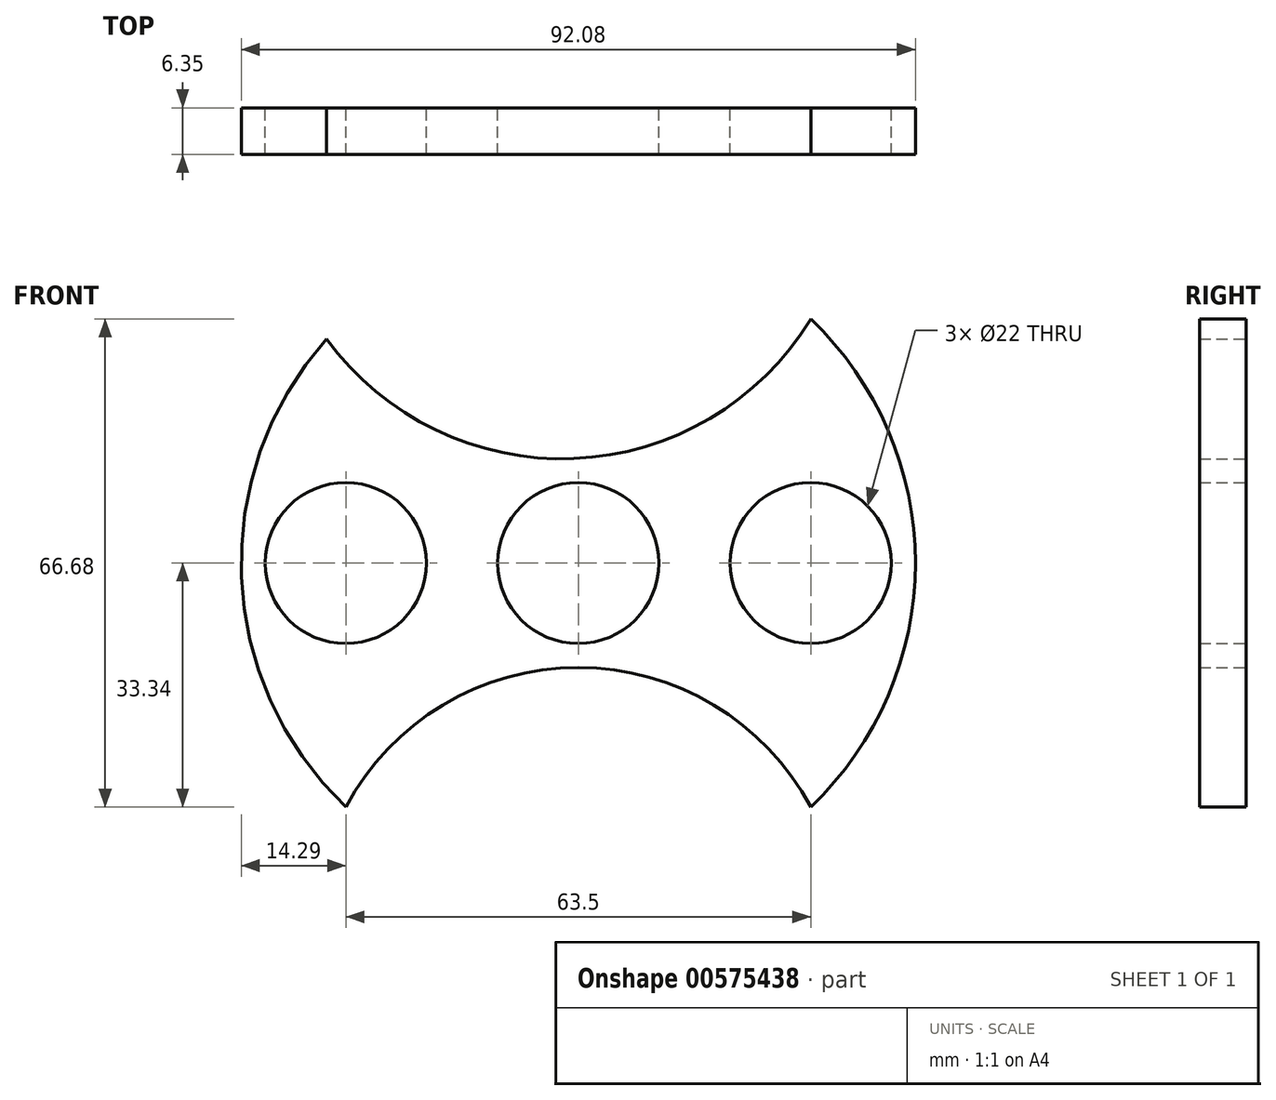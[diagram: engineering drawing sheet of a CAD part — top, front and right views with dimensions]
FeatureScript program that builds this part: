
annotation { "Feature Type Name" : "Feature", "Feature Type Description" : "" }
export const myFeature = defineFeature(function(context is Context, id is Id, definition is map)
    precondition{}
    {
        {
            var Q0;
            Q0=qCreatedBy(makeId("Front.planeOp"),FACE);
            var sketch = newSketch(context, id + "F0", { "sketchPlane" : qUnion([Q0])});
            skCircle(sketch, "E0", {"center": v(0, 0) * mm, "radius": 14.29 * mm});
            skCircle(sketch, "E1", {"center": v(0, 0) * mm, "radius": 11 * mm});
            skCircle(sketch, "E2", {"center": v(-31.75, 0) * mm, "radius": 14.29 * mm});
            skCircle(sketch, "E3", {"center": v(-31.75, 0) * mm, "radius": 11 * mm});
            skCircle(sketch, "E4.1.0", {"center": v(31.75, 0) * mm, "radius": 14.29 * mm});
            skCircle(sketch, "E4.1.1", {"center": v(31.75, 0) * mm, "radius": 11 * mm});
            skArc(sketch, "E5", {"start": v(-34.37, 30.63) * mm, "mid": v(-46, -1.88) * mm, "end": v(-31.75, -33.34) * mm});
            skArc(sketch, "E6", {"start": v(-34.37, 30.63) * mm, "mid": v(-0.58, 14.28) * mm, "end": v(31.75, 33.34) * mm});
            skArc(sketch, "E7", {"start": v(31.75, -33.34) * mm, "mid": v(0, -14.29) * mm, "end": v(-31.75, -33.34) * mm});
            skArc(sketch, "E8.trimOffspring", {"start": v(31.75, -33.34) * mm, "mid": v(46.04, 0) * mm, "end": v(31.75, 33.34) * mm});
            skSolve(sketch);
        }
        {
            var Q0;
            Q0 = qSketchRegion(id + "F0", true);
            extrude(context, id + "F1", {"entities" : qUnion([Q0]), "depth" : 6.35 * mm, "offsetDistance" : 25.4 * mm});
        }
    });
